# Revit family: Deca_Acabamento para registro de gaveta quadrada_Deca You_4900.105.PQ
name_source: partatom
category: Plumbing Fixtures
units: mm (PartAtom-declared; Revit-internal decimal feet)

## family parameters
Cut with Voids When Loaded = No
Host = Face
Part Type = Normal
Room Calculation Point = No
Round Connector Dimension = Use Radius
Shared = No

## types (7) — shared parameters
Acompanha o Produto = -
Aprovado por = quattroD
Atendimento ao Cliente = 0800-0117073
Categoria = Acabamento de Registro
Composição Básica = Liga de Cobre (Latão),Plásticos de Engenharia, Aço Inoxidavel e Elastômeros
Consumo = -
Cor Secundária = -
Criado por = quattroD
Default Elevation = 1.8 m
Itens de Instalação = -
Linha = Deca You
Manufacturer = DECA
Norma = Não possui
Pressão máx. funcionamento = -
Pressão mín. Aquec. Acúmulo = -
Pressão mín. Aquec. Passagem = -
Pressão mín. funcionamento = -
Saída de Esgoto = -
Segmento = Luxo
Tipo de dispositivo economizador = -
Tipo de mecanismo utilizado = -
Tipo de rosca de entrada = -
Tipo de rosca de saída = -
URL = www.deca.com.br
Vazão na Pressão máx. (L/min) = -
Vazão na Pressão mín. (L/min) = -
zero-valued in all types: CWFU, Diâmetro Ponto de Esgoto, Diâmetro Água Fria, Raio Ponto de Esgoto, Raio Água Fria, WFU

## per-type parameters (varying)
| type | Cor Principal | Código Pai | Material | Model | Peso Líquido (Kg) |
| 4900.C105.PQ_Cromado | Cromado | 4900.C105.PQ | Deca_Cromado | 4900.C105.PQ | 0 |
| 4900.BL105.PQ.MT_Black Matte | Black Matte | 4900.BL105.PQ.MT | Deca_Black Matte | 4900.BL105.PQ.MT | 0.635 |
| 4900.GF105.PQ.MT_Grafite | Antracite Dark | 4900.GF105.PQ.MT | Deca_Grafite | 4900.GF105.PQ.MT | 0 |
| 4900.INX105.PQ_Inox | Inox | 4900.INX105.PQ | Deca_Inox | 4900.INX105.PQ | 0 |
| 4900.MR105.PQ.MT_Brown Matte | BROWN MATTE | 4900.MR105.PQ.MT | Deca_Brown Matte | 4900.MR105.PQ.MT | 0 |
| 4900.SM105.PQ.MT_Summer Gold | SUMMER GOLD | 4900.SM105.PQ.MT | Deca_Summer Gold | 4900.SM105.PQ.MT | 0 |
| 4900.BR105.PQ.MT_Dynamic White | Dynamic White | 4900.BR105.PQ.MT | Deca_Dynamic White | 4900.BR105.PQ.MT | 0 |

## geometry (parser evidence)
native form markers: Sweep x2
no freeform markers — native parametric forms only
